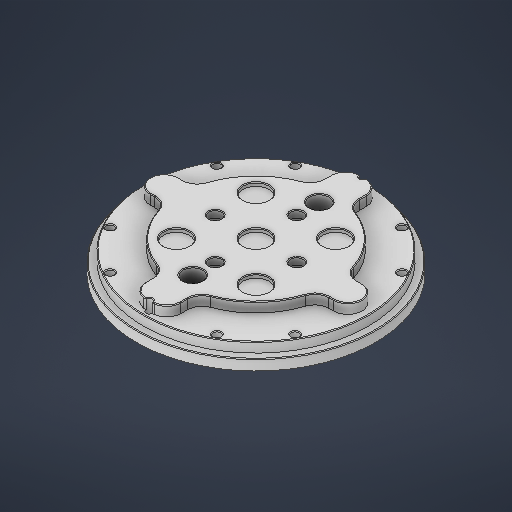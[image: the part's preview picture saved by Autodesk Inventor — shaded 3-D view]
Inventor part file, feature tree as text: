
AUTODESK INVENTOR PART (.ipt)
format: ipt  version: 2025 (Build 290162000, 162)  size: 651,776 bytes
history: native  units: in
note: dims shown in document units (in); Inventor stores cm internally (conversion verified against a paired STEP export)
features: sketch x14, extrude x10, hole x4, chamfer x4
ambient origin geometry x8: Origin, YZ Plane, XZ Plane, XY Plane, X Axis, Y Axis, Z Axis, Center Point
bodies: Solid1 (feature_tree)
feature tree (32):
  sketch  "Sketch1"  dims[d3=4.3307in d24=6.6929in]
  extrude  "Extrusion1"  Depth=6.6929in
  extrude  "Extrusion2"  Depth=5.9843in
  extrude  "Extrusion3"  Depth=4.3307in
  sketch  "Sketch2"  dims[d27=0.9843in d28=4.3307in]
  extrude  "Extrusion4"  Depth=0.3937in
  hole  "Hole1"  [1 undecoded]
  hole  "Hole2"  [1 undecoded]
  sketch  "Sketch4"  dims[d38=0.2953in d39=0.0in d40=2.2835in]
  extrude  "Extrusion5"  Depth=2.2835in
  extrude  "Extrusion6"  Depth=0.1969in
  hole  "Hole3"  [1 undecoded]
  chamfer  "Chamfer1"  Distance=0.7874in Angle=360.0deg
  chamfer  "Chamfer2"  Distance=0.1969in
  hole  "Hole5"  [1 undecoded]
  sketch  "Sketch8"  dims[d57=0.1378in d58=0.7874in d60=360.0deg]
  extrude  "Extrusion7"  Depth=0.0591in TaperAngle=0.0deg
  extrude  "Extrusion8"  Depth=0.0984in TaperAngle=0.0deg
  extrude  "Extrusion9"  Depth=0.0984in
  chamfer  "Chamfer3"  Distance=4.7244in Angle=360.0deg
  extrude  "Extrusion10"  Depth=0.0984in TaperAngle=45.0deg
  chamfer  "Chamfer4"  Distance=0.0197in Angle=45.0deg
  sketch  "Sketch Circular Pattern1"  dims[d25=6.2992in d26=5.9843in]
  sketch  "Sketch3"  dims[d31=0.3937in d32=0.3937in]
  sketch  "Sketch Circular Pattern2"  dims[d29=0.7874in d30=0.3937in]
  sketch  "Sketch5"  dims[d41=0.3543in d42=0.1969in]
  sketch  "Sketch Circular Pattern3"  dims[d34=0.8465in d35=0.0in d36=0.5709in d37=0.0in]
  sketch  "Sketch7"  dims[d56=5.9843in]
  sketch  "Sketch Circular Pattern5"  dims[d43=1.5748in d45=360.0deg d47=0.1969in d48=0.0in]
  sketch  "Sketch9"  dims[d62=0.1772in d63=0.315in d64=0.1575in d65=0.0787in d66=90.0deg d67=0.4646in d68=0.8108in]
  sketch  "Sketch Circular Pattern6"  dims[d49=0.2165in d50=0.7874in d51=0.1575in d52=0.0787in d53=90.0deg d54=0.315in d55=0.8108in]
  sketch  "Sketch10"  dims[d69=3.1496in d70=0.1969in d71=0.7874in d72=0.0591in d73=0.0in d74=0.4724in d75=0.0in d76=0.1969in d77=4.7244in d79=360.0deg d81=0.2165in d82=0.3937in d83=0.1575in d84=0.0787in d85=90.0deg d86=0.3937in d87=0.8108in d88=0.0197in d89=0.0787in d90=45.0deg d91=0.0197in d92=0.0787in d93=45.0deg d107=3.7402in d108=0.1969in d109=6.2992in d111=360.0deg d113=0.1969in d114=0.7874in d115=0.748in d116=0.3543in d117=90.0deg d118=0.7874in d119=0.8108in d120=0.3051in d121=0.3051in d122=0.3051in d123=0.3051in d125=0.3051in d126=0.3051in d127=0.3051in d128=0.3051in d129=0.3051in d130=0.3051in d131=0.3051in d132=0.3051in d133=0.2854in d134=0.2854in d135=0.1575in d136=0.0in d137=0.1378in d138=0.0in d139=0.7185in d140=3.1496in d141=0.7185in d142=3.1496in d144=360.0deg d146=0.0984in d147=0.0in d148=0.0197in d149=0.0787in d150=45.0deg d151=0.5512in d152=1.7717in d153=0.0in d154=0.0in d155=0.0197in d156=0.0787in d157=45.0deg d158=0.5512in d159=1.7717in]
note: 4 required parameter values undecoded (feature->parameter linkage not recoverable at this tier; creation-order binding heuristic only, values carry confidence <= 0.55)
